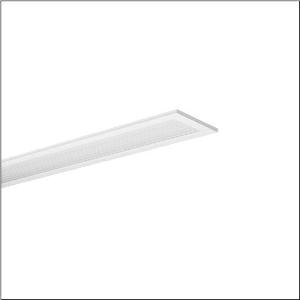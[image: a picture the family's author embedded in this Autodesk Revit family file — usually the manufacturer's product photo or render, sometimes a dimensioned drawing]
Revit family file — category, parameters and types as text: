
# Revit family: apollon_r__21_linear_51mq16wm2414_a263
name_source: partatom
category: Lighting Fixtures
units: mm (PartAtom-declared; Revit-internal decimal feet)

## family parameters
Cut with Voids When Loaded = No
Host = Face
Light Source = No
Part Type = Normal
Room Calculation Point = No
Round Connector Dimension = Use Diameter
Shared = No

## types (1)
- --- (1 x LED, 4380 lm, 29.4 W, 4000K)
    Apparent Load = 29 VA
    CIE Flux Codes = 64 88 97 100 100
    Color Rendering = 80
    Color Temperature = 4000K
    Default Elevation = 1800 mm
    Description = Apollon® 21 linear, office luminaire, primary optical cover: micro prismatic cover, of PMMA, CAT 2 (L<= 3000cd/m²), light emission: direct distribution, primary light characteristic: symmetric, installation type: lay-in mounting, LED, rated luminous flux: 3.520lm, luminous efficacy: 151lm/W, light colour: 840, colour temperature: 4000K, with terminal, 3-pole, mains connection: 220..240V, AC/DC, 0/50..60Hz, rated input power: 23.4W, housing, of aluminium, coated, traffic white (RAL 9016), length: 1.545mm, width: 179mm, height: 30mm, housing upper side, of sheet steel, galvanised, protection rating (complete): IP20, protection rating (lamp compartment, on room side): IP50, insulation class (complete): insulation class II (safety insulation), certification: CE, ENEC, impact resistance: IK03, permissible operating ambient temperature: -20..+45°C, permissible storage temperature: -40..+80°C, packaging unit: 1 piece
    Height = 0 mm  [stored 0 ft]
    Lamp = 1 x LED
    Lamp Light Flux = 4380 lm
    Lamp Power = 29.4 W
    Lamp count = 1
    Length = 1545 mm
    Luminous efficacy = 149 lm/W
    Manufacturer = Siteco
    ModVariant = No
    Model = 51MQ16WM2414
    Mounting Place = Ceiling
    Mounting Type = Recessed
    Number of Poles = 1
    OnlyDefault = Yes
    Power Factor = 1
    Product Name = Apollon® 21 linear
    Product group = office luminaire | ceiling recessed
    ProductGroupID = 401
    Protection Class = Protection class II
    Protection Degree = IP 20
    RLX_Detail_Level = 1
    RLX_Emergency_Light_Flux = 0 lm
    RLX_Emergency_Type = 0
    RLX_Emergency_Type_DB = No
    RlxData = <blob elided: 13865 chars, md5=673f366f>
    Socket = socket
    Standby Power = 0 W
    System Light Flux = 4380 lm
    System Power = 29 W
    Type Comments = factory setting: luminous flux: 100 % | (ON | ON | ON) | 700 mA
    Type Image = l_1291018.jpg
    URL = http://relux.com
    VarID = @adj_005677
    Voltage = 0 V
    Weight = 0.00 kg
    Width = 179 mm

note: [stored X ft] marks values corroborated as IEEE doubles in the binary element streams (Revit-internal decimal feet)

## geometry (parser evidence)
native form markers: Sweep x12
no freeform markers — native parametric forms only
